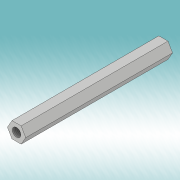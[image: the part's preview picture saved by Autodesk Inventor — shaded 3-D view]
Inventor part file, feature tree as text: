
AUTODESK INVENTOR PART (.ipt)
format: ipt  version: 2019 (Build 230136000, 136)  size: 102,400 bytes
history: native  units: mm
features: extrude x1, thread x1, sketch x1
ambient origin geometry x8: Origin, YZ Plane, XZ Plane, XY Plane, X Axis, Y Axis, Z Axis, Center Point
bodies: Solid1 (feature_tree)
feature tree (3):
  extrude  "Extrusion1"  Depth=10.0mm
  thread  "Thread3"  [1 undecoded]
  sketch  "Sketch1"  dims[d1=5.5mm d2=1.0mm d3=1.0mm d4=51.0mm d5=0.0mm d7=2.968mm d12=10.0mm d13=0.0mm]
note: 1 required parameter value undecoded (feature->parameter linkage not recoverable at this tier; creation-order binding heuristic only, values carry confidence <= 0.55)
